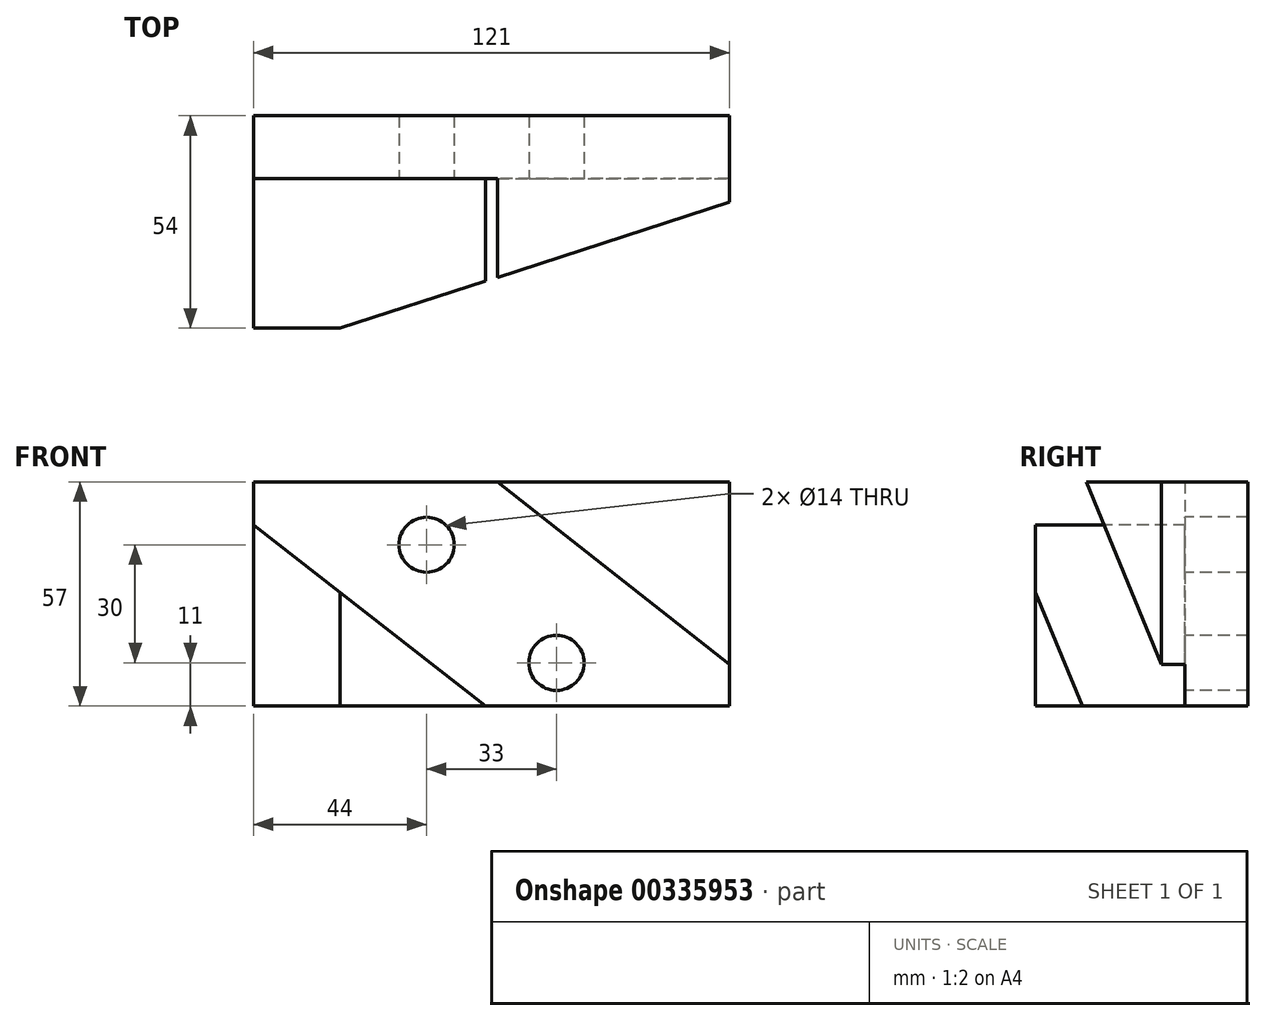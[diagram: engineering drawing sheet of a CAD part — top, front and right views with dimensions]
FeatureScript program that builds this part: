
annotation { "Feature Type Name" : "Feature", "Feature Type Description" : "" }
export const myFeature = defineFeature(function(context is Context, id is Id, definition is map)
    precondition{}
    {
        {
            var Q0;
            Q0=qCreatedBy(makeId("Top.planeOp"),FACE);
            var sketch = newSketch(context, id + "F0", { "sketchPlane" : qUnion([Q0])});
            skLineSegment(sketch, "E0", {"start": v(0, 0) * mm, "end": v(0, 54) * mm});
            skLineSegment(sketch, "E1", {"start": v(0, 54) * mm, "end": v(121, 54) * mm});
            skLineSegment(sketch, "E2", {"start": v(121, 54) * mm, "end": v(121, 32) * mm});
            skLineSegment(sketch, "E3", {"start": v(121, 32) * mm, "end": v(22, 0) * mm});
            skLineSegment(sketch, "E4", {"start": v(22, 0) * mm, "end": v(0, 0) * mm});
            skSolve(sketch);
        }
        {
            var Q0;
            Q0 = qSketchRegion(id + "F0", true);
            extrude(context, id + "F1", {"entities" : qUnion([Q0]), "endBound" : BoundingType.SYMMETRIC, "depth" : 57 * mm});
        }
        {
            var Q0;
            Q0=makeQuery(id+"F1.opExtrude","SWEPT_FACE",FACE,{"disambiguationData":[OSD([sQuery(id+"F0.wireOp",EDGE,"E4")])]});
            var sketch = newSketch(context, id + "F2", { "sketchPlane" : qUnion([Q0])});
            skLineSegment(sketch, "E5", {"start": v(0, 28.5) * mm, "end": v(0, 17.5) * mm});
            skLineSegment(sketch, "E6", {"start": v(0, 28.5) * mm, "end": v(62, 28.5) * mm});
            skLineSegment(sketch, "E7", {"start": v(62, 28.5) * mm, "end": v(121, -17.97) * mm});
            skLineSegment(sketch, "E8", {"start": v(121, -28.5) * mm, "end": v(121, -17.97) * mm});
            skLineSegment(sketch, "E9", {"start": v(121, -28.5) * mm, "end": v(59, -28.5) * mm});
            skLineSegment(sketch, "E10", {"start": v(59, -28.5) * mm, "end": v(0, 17.5) * mm});
            skSolve(sketch);
        }
        {
            var Q0;
            Q0 = qSketchRegion(id + "F2", true);
            extrude(context, id + "F3", {"entities" : qUnion([Q0]), "operationType" : NewBodyOperationType.REMOVE, "oppositeDirection" : true, "depth" : 38 * mm});
        }
        {
            var Q0;
            Q0=makeQuery(id+"F3.boolean.opBoolean","COPY",FACE,{"derivedFrom":makeQuery(id+"F3.opExtrude","CAP_FACE",FACE,{"disambiguationData":[OSD([sQuery(id+"F2.wireOp",EDGE,"E5"),sQuery(id+"F2.wireOp",EDGE,"E6"),sQuery(id+"F2.wireOp",EDGE,"E7"),sQuery(id+"F2.wireOp",EDGE,"E8"),sQuery(id+"F2.wireOp",EDGE,"E9"),sQuery(id+"F2.wireOp",EDGE,"E10")])],"isStart":false})});
            var sketch = newSketch(context, id + "F4", { "sketchPlane" : qUnion([Q0])});
            skLineSegment(sketch, "E11", {"start": v(0, 28.5) * mm, "end": v(44, 28.5) * mm, "construction": true});
            skLineSegment(sketch, "E12", {"start": v(44, 28.5) * mm, "end": v(44, 12.5) * mm, "construction": true});
            skCircle(sketch, "E13", {"center": v(44, 12.5) * mm, "radius": 7 * mm});
            skLineSegment(sketch, "E14", {"start": v(44, 28.5) * mm, "end": v(77, 28.5) * mm, "construction": true});
            skLineSegment(sketch, "E15", {"start": v(77, 28.5) * mm, "end": v(77, -17.5) * mm, "construction": true});
            skCircle(sketch, "E16", {"center": v(77, -17.5) * mm, "radius": 7 * mm});
            skSolve(sketch);
        }
        {
            var Q0;
            Q0 = qSketchRegion(id + "F4", true);
            extrude(context, id + "F5", {"entities" : qUnion([Q0]), "operationType" : NewBodyOperationType.REMOVE, "oppositeDirection" : true, "depth" : 25 * mm});
        }
    });
